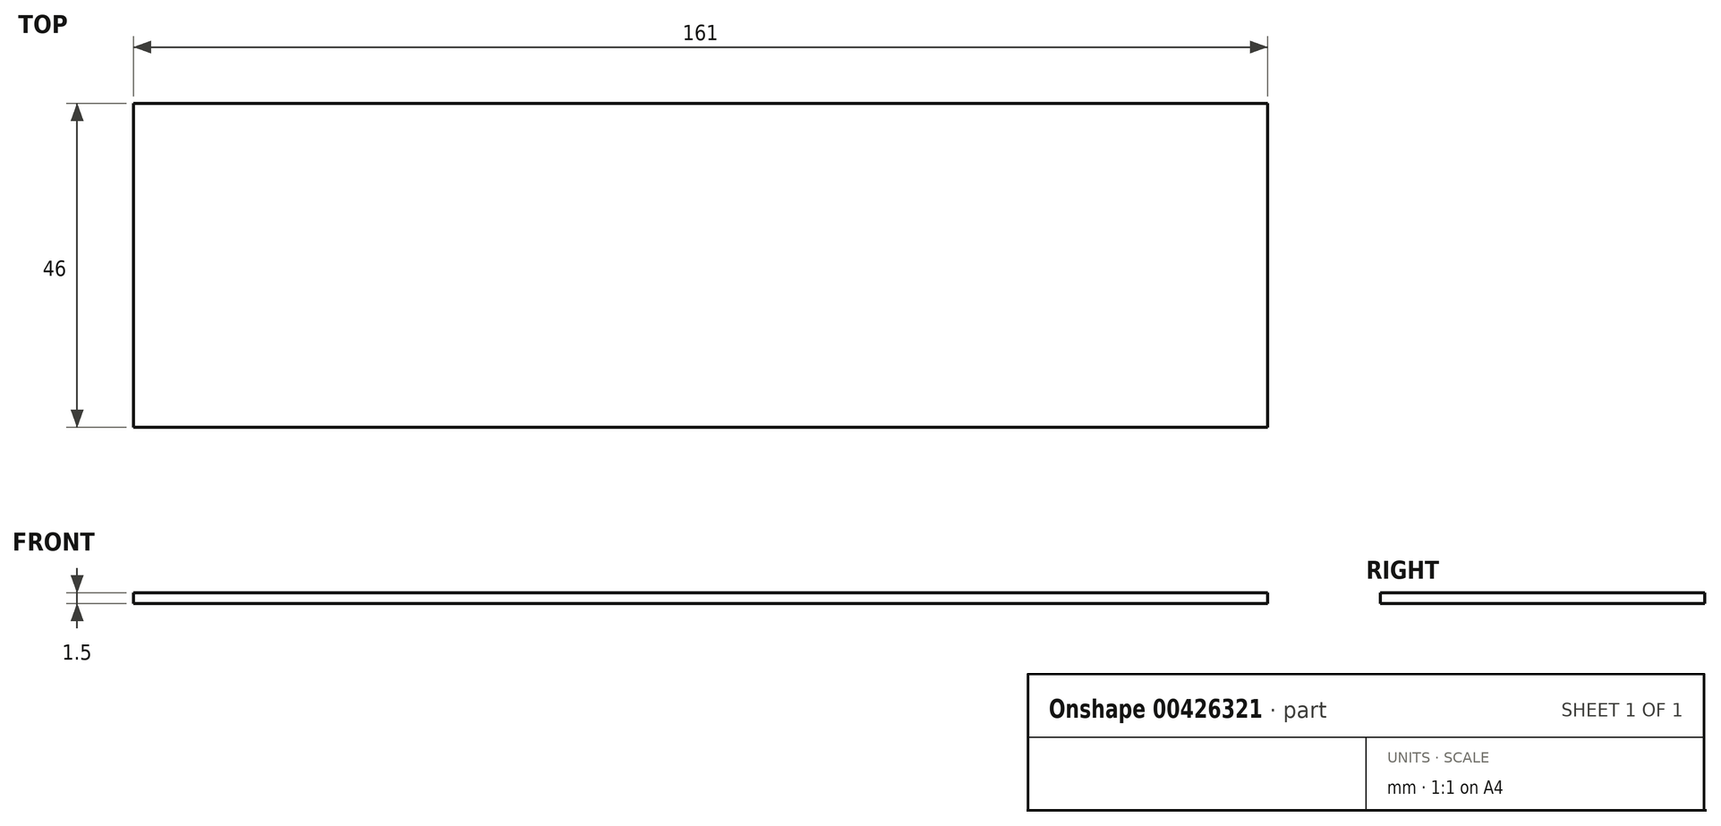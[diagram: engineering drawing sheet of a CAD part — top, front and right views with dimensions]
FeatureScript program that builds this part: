
annotation { "Feature Type Name" : "Feature", "Feature Type Description" : "" }
export const myFeature = defineFeature(function(context is Context, id is Id, definition is map)
    precondition{}
    {
        {
            var Q0;
            Q0=qCreatedBy(makeId("Top.planeOp"),FACE);
            var sketch = newSketch(context, id + "F0", { "sketchPlane" : qUnion([Q0])});
            skLineSegment(sketch, "E0.bottom", {"start": v(80.5, 23) * mm, "end": v(-80.5, 23) * mm});
            skLineSegment(sketch, "E0.top", {"start": v(80.5, -23) * mm, "end": v(-80.5, -23) * mm});
            skLineSegment(sketch, "E0.left", {"start": v(80.5, 23) * mm, "end": v(80.5, -23) * mm});
            skLineSegment(sketch, "E0.right", {"start": v(-80.5, 23) * mm, "end": v(-80.5, -23) * mm});
            skPoint(sketch, "E0.middle", {"position": v(0, 0) * mm});
            skSolve(sketch);
        }
        {
            var Q0;
            Q0 = qSketchRegion(id + "F0", true);
            extrude(context, id + "F1", {"entities" : qUnion([Q0]), "depth" : 1.5 * mm, "offsetDistance" : 25 * mm});
        }
    });
